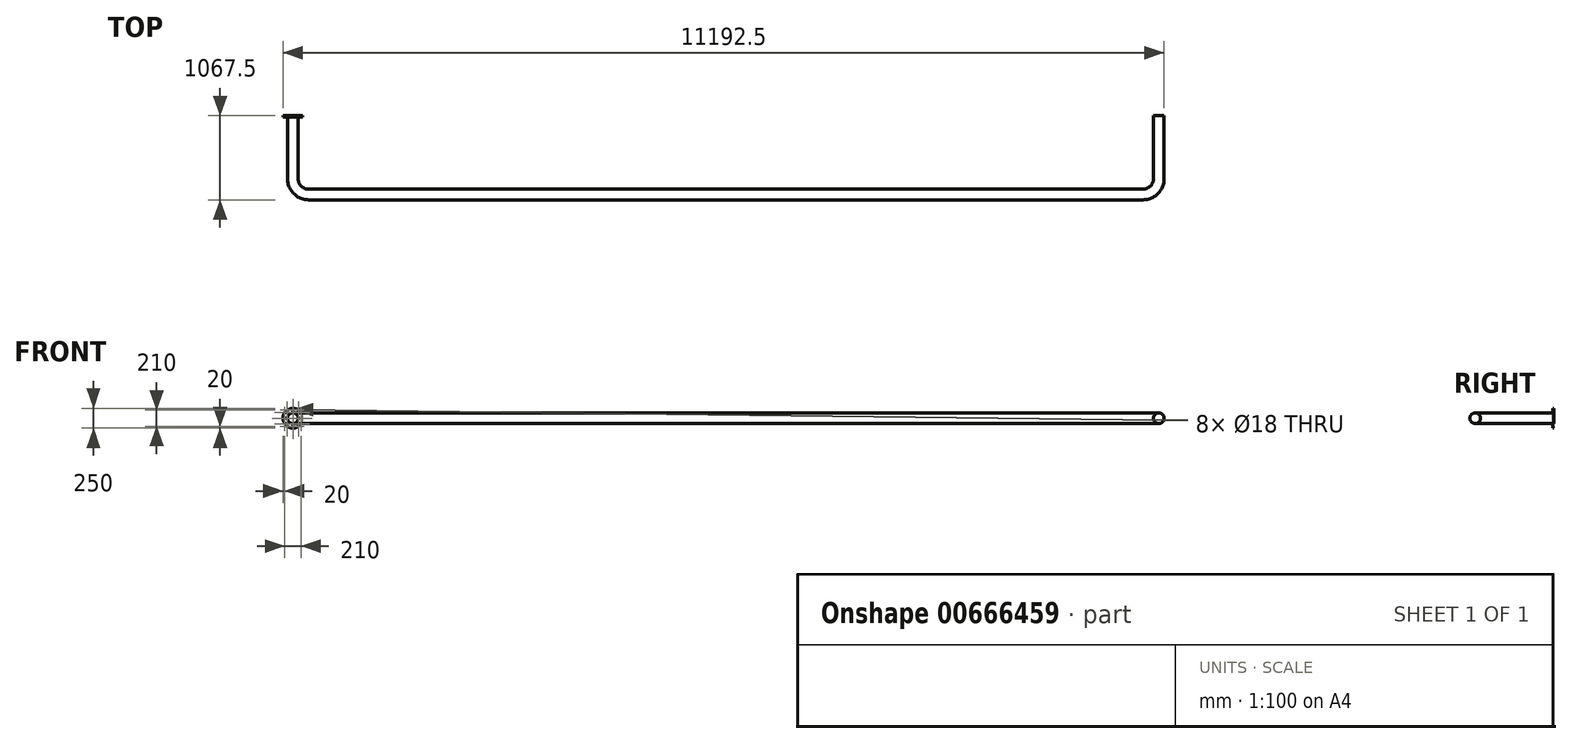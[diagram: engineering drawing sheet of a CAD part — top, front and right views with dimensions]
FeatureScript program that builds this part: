
annotation { "Feature Type Name" : "Feature", "Feature Type Description" : "" }
export const myFeature = defineFeature(function(context is Context, id is Id, definition is map)
    precondition{}
    {
        {
            var Q0;
            Q0=qCreatedBy(makeId("Top.planeOp"),FACE);
            var sketch = newSketch(context, id + "F0", { "sketchPlane" : qUnion([Q0])});
            skLineSegment(sketch, "E0", {"start": v(200, 0) * mm, "end": v(10800, 0) * mm});
            skLineSegment(sketch, "E1", {"start": v(0, 200) * mm, "end": v(0, 1000) * mm});
            skLineSegment(sketch, "E2", {"start": v(11000, 200) * mm, "end": v(11000, 1000) * mm});
            skPoint(sketch, "E3.visualSharp", {"position": v(11000, 0) * mm});
            skArc(sketch, "E3.filletArc", {"start": v(10800, 0) * mm, "mid": v(10941.42, 58.58) * mm, "end": v(11000, 200) * mm});
            skPoint(sketch, "E4.visualSharp", {"position": v(0, 0) * mm});
            skArc(sketch, "E4.filletArc", {"start": v(0, 200) * mm, "mid": v(58.58, 58.58) * mm, "end": v(200, 0) * mm});
            skSolve(sketch);
        }
        {
            var Q0;
            Q0=qCreatedBy(makeId("Front.planeOp"),FACE);
            cPlane(context, id + "F1", {"entities" : qUnion([Q0]), "cplaneType" : CPlaneType.OFFSET, "offset" : 1000 * mm, "oppositeDirection" : true, "width" : 150 * mm, "height" : 150 * mm});
        }
        {
            var Q0;
            Q0=qCreatedBy(id+"F1.planeOp",FACE);
            var sketch = newSketch(context, id + "F2", { "sketchPlane" : qUnion([Q0])});
            skPoint(sketch, "E5.0", {"position": v(0, 0) * mm});
            skCircle(sketch, "E6", {"center": v(0, 0) * mm, "radius": 67.5 * mm});
            skCircle(sketch, "E7", {"center": v(0, 0) * mm, "radius": 125 * mm});
            skCircle(sketch, "E8", {"center": v(0, -105) * mm, "radius": 9 * mm});
            skCircle(sketch, "E9.1.0", {"center": v(74.25, -74.25) * mm, "radius": 9 * mm});
            skCircle(sketch, "E9.2.0", {"center": v(105, 0) * mm, "radius": 9 * mm});
            skCircle(sketch, "E9.3.0", {"center": v(74.25, 74.25) * mm, "radius": 9 * mm});
            skCircle(sketch, "E9.4.0", {"center": v(0, 105) * mm, "radius": 9 * mm});
            skCircle(sketch, "E9.5.0", {"center": v(-74.25, 74.25) * mm, "radius": 9 * mm});
            skCircle(sketch, "E9.6.0", {"center": v(-105, 0) * mm, "radius": 9 * mm});
            skCircle(sketch, "E9.7.0", {"center": v(-74.25, -74.25) * mm, "radius": 9 * mm});
            skSolve(sketch);
        }
        {
            var Q0;
            Q0=makeQuery(id+"F2.imprint","IMPRINT",FACE,{"disambiguationData":[TD([[makeQuery(id+"F2.imprint","IMPRINT",EDGE,{"derivedFrom":sQuery(id+"F2.wireOp",EDGE,"E6")}),1.0]])]});
            var Q1;
            Q1=sQuery(id+"F0.wireOp",EDGE,"E1");
            var Q2;
            Q2=sQuery(id+"F0.wireOp",EDGE,"E4.filletArc");
            var Q3;
            Q3=sQuery(id+"F0.wireOp",EDGE,"E0");
            var Q4;
            Q4=sQuery(id+"F0.wireOp",EDGE,"E3.filletArc");
            var Q5;
            Q5=sQuery(id+"F0.wireOp",EDGE,"E2");
            sweep(context, id + "F3", {"profiles" : qUnion([Q0]), "path" : qUnion([Q1, Q2, Q3, Q4, Q5])});
        }
        {
            var Q0;
            Q0 = qSketchRegion(id + "F2", true);
            var Q1;
            Q1=makeQuery(id+"F3.opSweep","CAP_FACE",FACE,{"disambiguationData":[OSD([sQuery(id+"F0.wireOp",VERTEX,"E1.end"),sQuery(id+"F2.wireOp",EDGE,"E6")])],"isStart":true});
            extrude(context, id + "F4", {"entities" : qUnion([Q0, Q1]), "operationType" : NewBodyOperationType.ADD, "depth" : 15 * mm, "offsetDistance" : 25 * mm});
        }
    });
